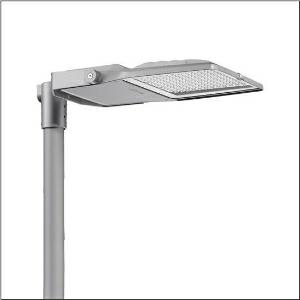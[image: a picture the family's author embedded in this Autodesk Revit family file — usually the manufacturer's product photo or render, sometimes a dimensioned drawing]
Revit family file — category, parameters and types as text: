
# Revit family: floodlight_fl_21_midi___pl33t_5xa7786f2f3a_5712
name_source: partatom
category: Lighting Fixtures
units: mm (PartAtom-declared; Revit-internal decimal feet)

## family parameters
Cut with Voids When Loaded = No
Host = Face
Light Source = No
Part Type = Normal
Room Calculation Point = No
Round Connector Dimension = Use Diameter
Shared = No

## types (1)
- --- (1 x LED, 35340 lm, 271.6 W, 3000K)
    Apparent Load = 272 VA
    CIE Flux Codes = 26 75 99 100 100
    Color Rendering = 70
    Color Temperature = 3000K
    Default Elevation = 1800 mm
    Description = Floodlight FL 21 midi, floodlight, primary light control with lens, of PMMA, primary optical cover: protective disc, of toughened safety glass, transparent, light distribution: PL33T, light emission: direct distribution, installation type: surface-mounted, LED, High Power LED, rated luminous flux: 35.340lm, luminous efficacy: 130lm/W, light colour: 730, colour temperature: 3000K, control gear: Smart Interface (Zhaga), control: flexible luminous flux parameterisation, time-dependent luminous flux control, constant luminous flux control, overheat protection, pre-setting: logarithmic dimming characteristic, with terminal, 6-pole, mains connection: 220..240V, AC, 50/60Hz, start of lifetime: 272W, end of service life: 287W, reduction: 123W, luminaire housing, of diecast aluminium, powder-coated, Siteco® metallic grey (DB 702S), corrosivity category C5 mid according to DIN EN ISO 12944, suitable for swimming pools, chlorine-resistant, sealing non-destructively replaceable, please order mast flange separately, mast bracket, of steel, galvanised, powder-coated, Siteco® metallic grey (DB 702S), Smart Interface below and above, protection rating (complete): IP66, insulation class (complete): insulation class II (safety insulation), certification: CE, ENEC, VDE, protection symbol: D, impact resistance: IK08, permissible operating ambient temperature: -40..+40°C, permissible operating ambient temperature for outdoor applications: -40..+50°C, standard: DIN EN 12944, LABS conformity tested according to VDMA 24364:2018-05, packaging unit: 1 piece

Light Distribution: PL33T
    Height = 76 mm
    Lamp = 1 x LED
    Lamp Light Flux = 35340 lm
    Lamp Power = 271.6 W
    Lamp count = 1
    Length = 657 mm
    Luminous efficacy = 130 lm/W
    Manufacturer = Siteco
    ModVariant = No
    Model = 5XA7786F2F3A
    Number of Poles = 1
    OnlyDefault = Yes
    Power Factor = 1
    Product Name = Floodlight FL 21 midi | PL33T
    Product group = floodlight | pylon annexe
    ProductGroupID = 6200
    Protection Class = Protection class II
    Protection Degree = IP 66
    RLX_Detail_Level = 1
    RLX_Emergency_Light_Flux = 0 lm
    RLX_Emergency_Type = 0
    RLX_Emergency_Type_DB = No
    RlxData = <blob elided: 153649 chars, md5=2e9133ee>
    Socket = socket
    Standby Power = 0 W
    System Light Flux = 35340 lm
    System Power = 272 W
    Type Comments = factory setting: luminous flux: 100 % | dim-lin: 254 | 620 mA
    Type Image = l_1007123.jpg
    URL = http://relux.com
    VarID = @adj_150392
    Voltage = 0 V
    Weight = 0.00 kg
    Width = 442 mm

## geometry (parser evidence)
native form markers: Blend x4, Sweep x13
no freeform markers — native parametric forms only
